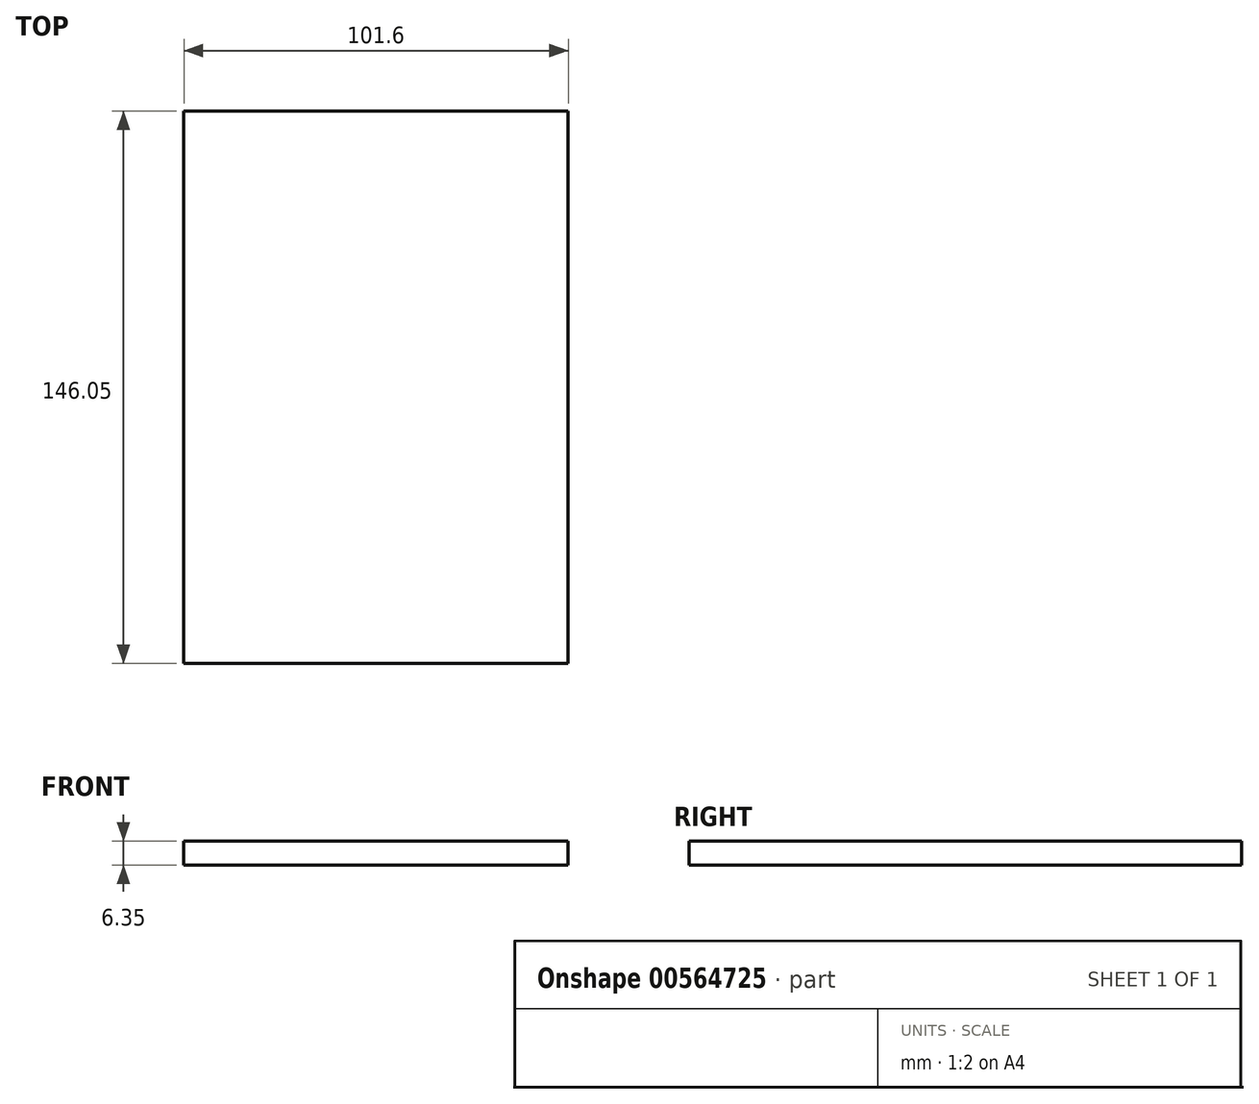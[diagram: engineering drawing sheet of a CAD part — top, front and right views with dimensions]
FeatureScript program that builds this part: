
annotation { "Feature Type Name" : "Feature", "Feature Type Description" : "" }
export const myFeature = defineFeature(function(context is Context, id is Id, definition is map)
    precondition{}
    {
        {
            var Q0;
            Q0=qCreatedBy(makeId("Top.planeOp"),FACE);
            var sketch = newSketch(context, id + "F0", { "sketchPlane" : qUnion([Q0])});
            skLineSegment(sketch, "E0.bottom", {"start": v(-59.47, 73.04) * mm, "end": v(42.13, 73.04) * mm});
            skLineSegment(sketch, "E0.top", {"start": v(-59.47, -73.01) * mm, "end": v(42.13, -73.01) * mm});
            skLineSegment(sketch, "E0.left", {"start": v(-59.47, 73.04) * mm, "end": v(-59.47, -73.01) * mm});
            skLineSegment(sketch, "E0.right", {"start": v(42.13, 73.04) * mm, "end": v(42.13, -73.01) * mm});
            skSolve(sketch);
        }
        {
            var Q0;
            Q0=makeQuery(id+"F0.imprint","IMPRINT",FACE,{"disambiguationData":[TD([[makeQuery(id+"F0.imprint","IMPRINT",EDGE,{"derivedFrom":sQuery(id+"F0.wireOp",EDGE,"E0.bottom")}),-1.0]])]});
            extrude(context, id + "F1", {"entities" : qUnion([Q0]), "depth" : 6.35 * mm, "offsetDistance" : 25.4 * mm});
        }
    });
